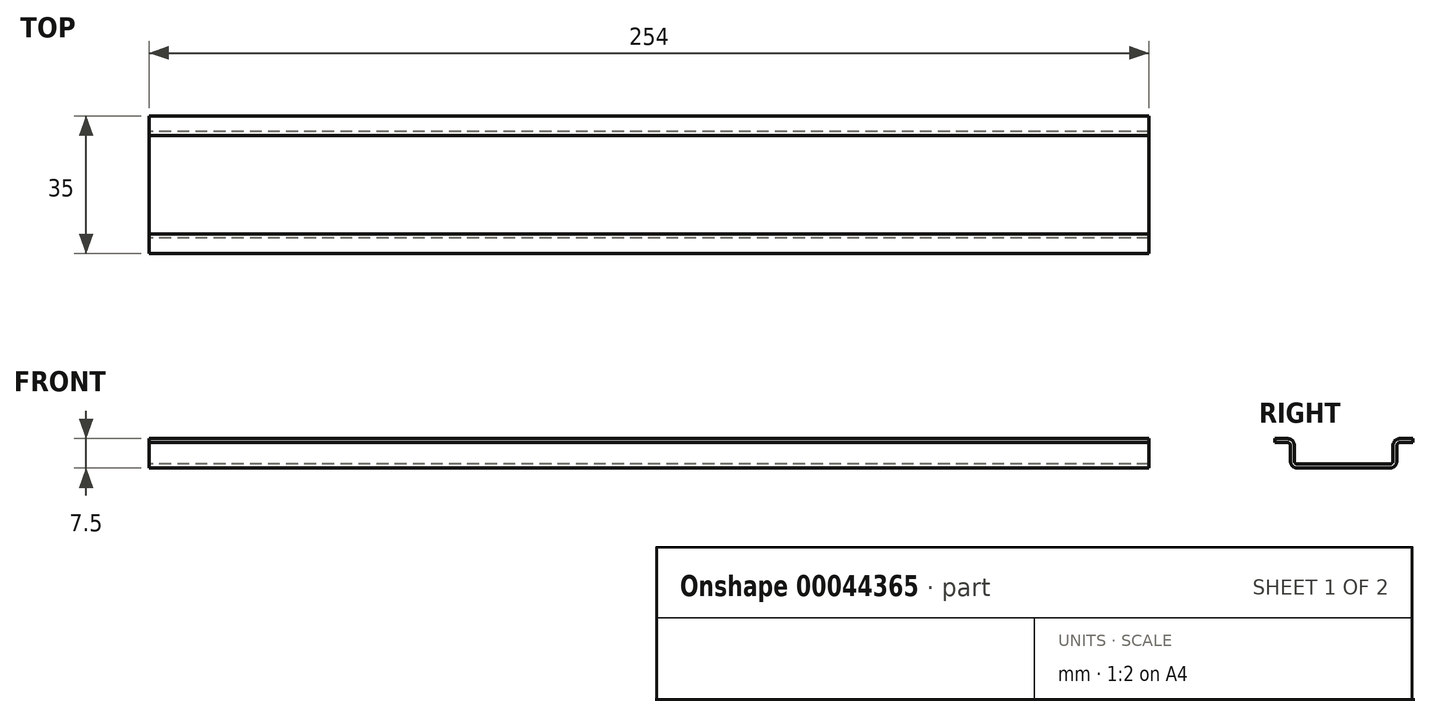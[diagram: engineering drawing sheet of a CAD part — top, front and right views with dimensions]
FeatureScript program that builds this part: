
annotation { "Feature Type Name" : "Feature", "Feature Type Description" : "" }
export const myFeature = defineFeature(function(context is Context, id is Id, definition is map)
    precondition{}
    {
        {
            var Q0;
            Q0=qCreatedBy(makeId("Right.planeOp"),FACE);
            var sketch = newSketch(context, id + "F0", { "sketchPlane" : qUnion([Q0])});
            skLineSegment(sketch, "E0", {"start": v(10.52, 64.63) * mm, "end": v(10.52, 68.53) * mm});
            skLineSegment(sketch, "E1", {"start": v(-13.73, 63.83) * mm, "end": v(9.72, 63.83) * mm});
            skLineSegment(sketch, "E2", {"start": v(-14.53, 68.53) * mm, "end": v(-14.53, 64.63) * mm});
            skLineSegment(sketch, "E3", {"start": v(-19.48, 70.33) * mm, "end": v(-16.33, 70.33) * mm});
            skLineSegment(sketch, "E4", {"start": v(-19.48, 69.33) * mm, "end": v(-19.48, 70.33) * mm});
            skLineSegment(sketch, "E5", {"start": v(15.52, 70.33) * mm, "end": v(15.52, 69.33) * mm});
            skLineSegment(sketch, "E6", {"start": v(12.32, 70.33) * mm, "end": v(15.52, 70.33) * mm});
            skLineSegment(sketch, "E7", {"start": v(-19.48, 69.33) * mm, "end": v(-16.33, 69.33) * mm});
            skLineSegment(sketch, "E8", {"start": v(-15.53, 68.53) * mm, "end": v(-15.53, 64.63) * mm});
            skLineSegment(sketch, "E9", {"start": v(-13.73, 62.83) * mm, "end": v(9.72, 62.83) * mm});
            skLineSegment(sketch, "E10", {"start": v(11.52, 64.63) * mm, "end": v(11.52, 68.53) * mm});
            skLineSegment(sketch, "E11", {"start": v(12.32, 69.33) * mm, "end": v(15.52, 69.33) * mm});
            skArc(sketch, "E12", {"start": v(-15.53, 68.53) * mm, "mid": v(-15.76, 69.1) * mm, "end": v(-16.33, 69.33) * mm});
            skArc(sketch, "E13", {"start": v(-14.53, 64.63) * mm, "mid": v(-14.3, 64.06) * mm, "end": v(-13.73, 63.83) * mm});
            skArc(sketch, "E14", {"start": v(9.72, 63.83) * mm, "mid": v(10.29, 64.06) * mm, "end": v(10.52, 64.63) * mm});
            skArc(sketch, "E15", {"start": v(12.32, 69.33) * mm, "mid": v(11.76, 69.1) * mm, "end": v(11.52, 68.53) * mm});
            skArc(sketch, "E16", {"start": v(-14.53, 68.53) * mm, "mid": v(-15.06, 69.8) * mm, "end": v(-16.33, 70.33) * mm});
            skArc(sketch, "E17", {"start": v(-15.53, 64.63) * mm, "mid": v(-15, 63.35) * mm, "end": v(-13.73, 62.83) * mm});
            skArc(sketch, "E18", {"start": v(9.72, 62.83) * mm, "mid": v(11, 63.35) * mm, "end": v(11.52, 64.63) * mm});
            skArc(sketch, "E19", {"start": v(12.32, 70.33) * mm, "mid": v(11.05, 69.8) * mm, "end": v(10.52, 68.53) * mm});
            skSolve(sketch);
        }
        {
            var Q0;
            Q0 = qSketchRegion(id + "F0", true);
            var Q1;
            Q1=makeQuery(id+"F0.imprint","IMPRINT",FACE,{"disambiguationData":[TD([[makeQuery(id+"F0.imprint","IMPRINT",EDGE,{"derivedFrom":sQuery(id+"F0.wireOp",EDGE,"E0")}),-1.0]])]});
            extrude(context, id + "F1", {"entities" : qUnion([Q0, Q1]), "endBound" : BoundingType.SYMMETRIC, "depth" : 254 * mm});
        }
    });
